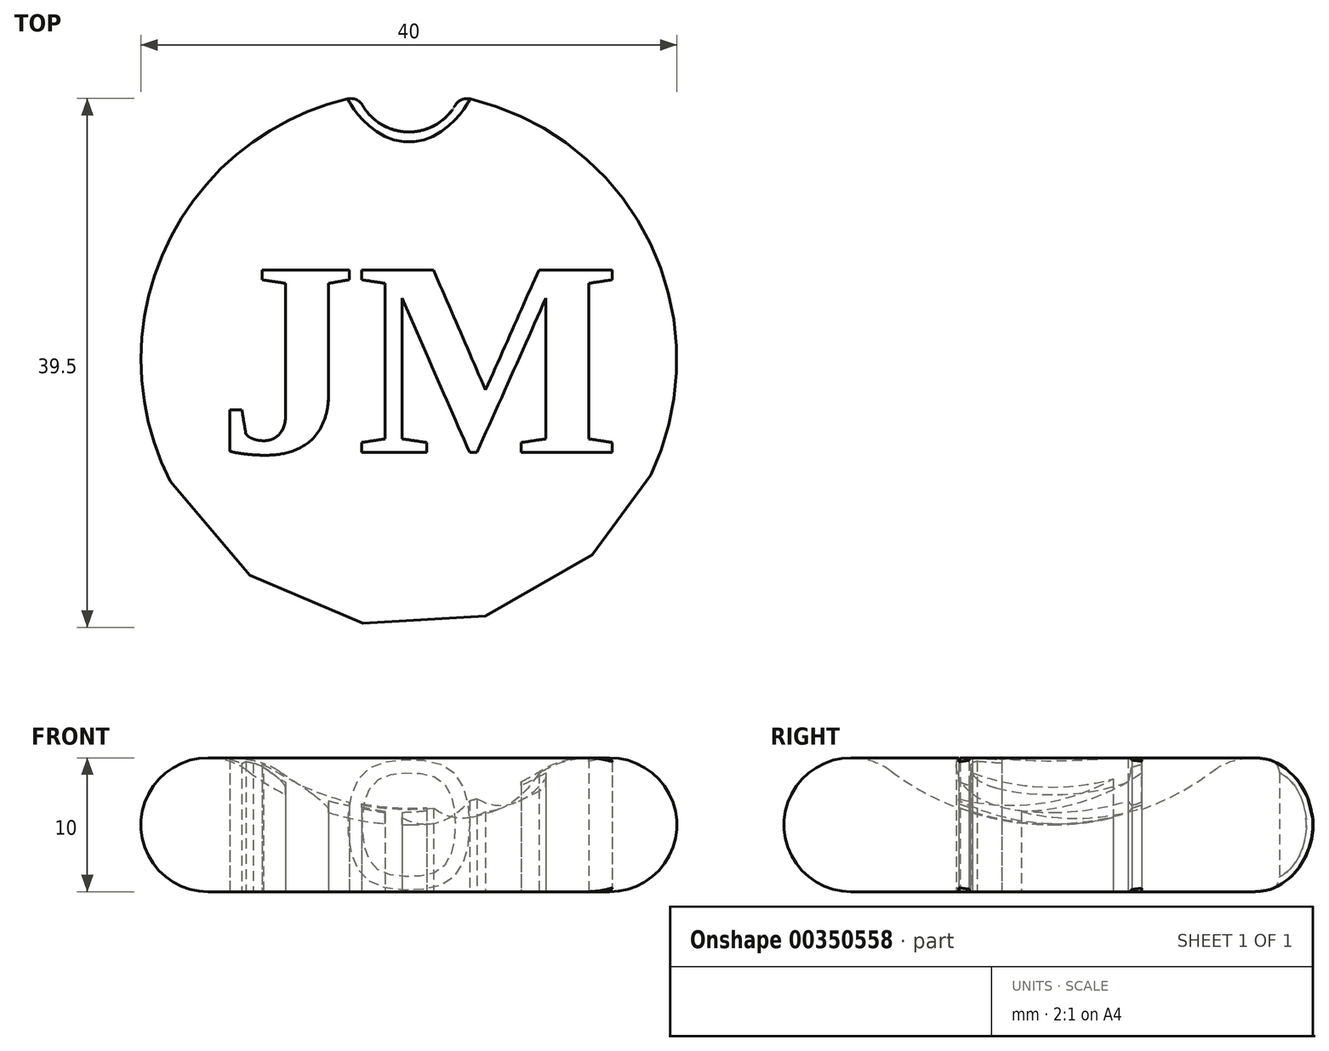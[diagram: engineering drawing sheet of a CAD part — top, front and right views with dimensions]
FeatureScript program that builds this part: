
annotation { "Feature Type Name" : "Feature", "Feature Type Description" : "" }
export const myFeature = defineFeature(function(context is Context, id is Id, definition is map)
    precondition{}
    {
        {
            var Q0;
            Q0=qCreatedBy(makeId("Front.planeOp"),FACE);
            var sketch = newSketch(context, id + "F0", { "sketchPlane" : qUnion([Q0])});
            skArc(sketch, "E0", {"start": v(-12, 9) * mm, "mid": v(-19.74, 6.58) * mm, "end": v(-15, 0) * mm});
            skArc(sketch, "E1", {"start": v(-12, 9) * mm, "mid": v(-6.32, 6.03) * mm, "end": v(0, 5) * mm});
            skLineSegment(sketch, "E2", {"start": v(-15, 0) * mm, "end": v(0, 0) * mm});
            skLineSegment(sketch, "E3", {"start": v(0, 0) * mm, "end": v(0, 5) * mm});
            skSolve(sketch);
        }
        {
            var Q0;
            Q0=makeQuery(id+"F0.imprint","IMPRINT",FACE,{"disambiguationData":[TD([[makeQuery(id+"F0.imprint","IMPRINT",EDGE,{"derivedFrom":sQuery(id+"F0.wireOp",EDGE,"E0")}),1.0]])]});
            var Q1;
            Q1=sQuery(id+"F0.wireOp",EDGE,"E3");
            revolve(context, id + "F1", {"entities" : qUnion([Q0]), "axis" : qUnion([Q1]), "revolveType" : RevolveType.FULL});
        }
        {
            var Q0;
            Q0=qCreatedBy(makeId("Top.planeOp"),FACE);
            var sketch = newSketch(context, id + "F2", { "sketchPlane" : qUnion([Q0])});
            skText(sketch, "E4", { "text": "JM", "fontName": "Tinos-Bold.ttf"});
            const initialGuessF2  = {"E4": [-0.0143, -0.00694, 1, 0, 0.015]};
            skSetInitialGuess(sketch, initialGuessF2);
            skSolve(sketch);
        }
        {
            var Q0;
            Q0 = qSketchRegion(id + "F2", true);
            extrude(context, id + "F3", {"entities" : qUnion([Q0]), "operationType" : NewBodyOperationType.REMOVE, "oppositeDirection" : true, "depth" : 50 * mm});
        }
        {
            var Q0;
            Q0 = qSketchRegion(id + "F2", true);
            extrude(context, id + "F4", {"entities" : qUnion([Q0]), "operationType" : NewBodyOperationType.REMOVE, "oppositeDirection" : true, "depth" : -25 * mm});
        }
        {
            var Q0;
            Q0=qCreatedBy(makeId("Top.planeOp"),FACE);
            var sketch = newSketch(context, id + "F5", { "sketchPlane" : qUnion([Q0])});
            skCircle(sketch, "E5", {"center": v(0, 21) * mm, "radius": 4 * mm});
            skSolve(sketch);
        }
        {
            var Q0;
            Q0=makeQuery(id+"F5.imprint","IMPRINT",FACE,{"disambiguationData":[TD([[makeQuery(id+"F5.imprint","IMPRINT",EDGE,{"derivedFrom":sQuery(id+"F5.wireOp",EDGE,"E5")}),1.0]])]});
            var Q1;
            Q1=sQuery(id+"F5.wireOp",EDGE,"E5");
            extrude(context, id + "F6", {"entities" : qUnion([Q0]), "operationType" : NewBodyOperationType.REMOVE, "surfaceEntities" : qUnion([Q1]), "oppositeDirection" : true, "depth" : -25 * mm});
        }
        {
            var Q0;
            Q0=makeQuery(id+"F6.boolean.opBoolean","INTERSECT",EDGE,{"derivedFrom":[makeQuery(id+"F1.opRevolve","SWEPT_FACE",FACE,{"disambiguationData":[OSD([sQuery(id+"F0.wireOp",EDGE,"E0")])]}),makeQuery(id+"F6.opExtrude","SWEPT_FACE",FACE,{"disambiguationData":[OSD([sQuery(id+"F5.wireOp",EDGE,"E5")])]})]});
            fillet(context, id + "F7", {"entities" : qUnion([Q0]), "radius" : 1 * mm, "tangentPropagation" : true, "allowEdgeOverflow" : false});
        }
    });
